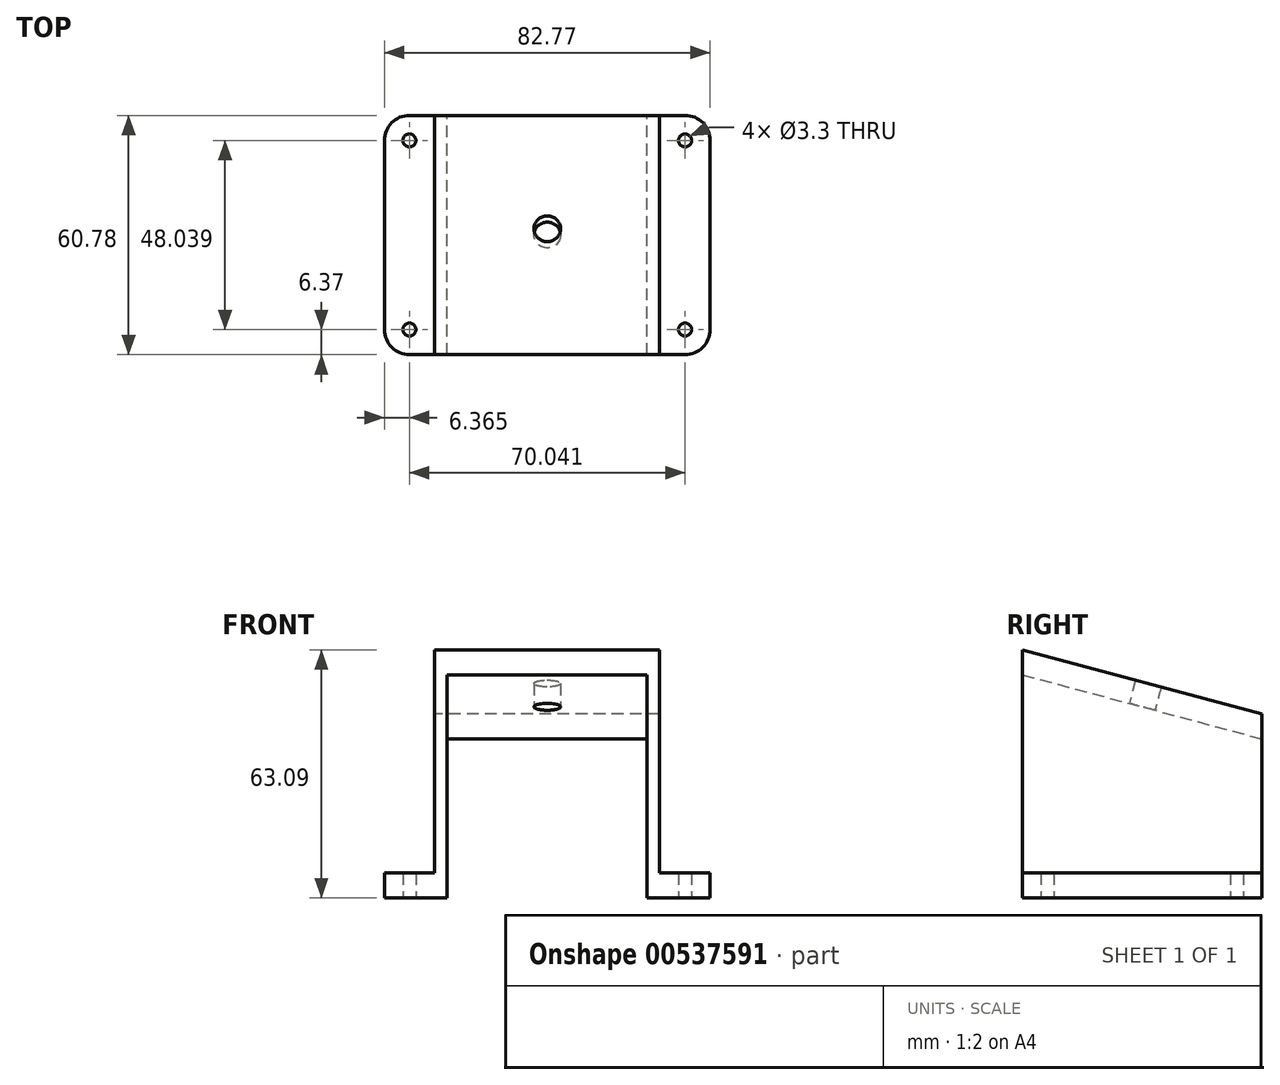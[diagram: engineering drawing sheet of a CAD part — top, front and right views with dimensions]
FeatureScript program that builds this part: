
annotation { "Feature Type Name" : "Feature", "Feature Type Description" : "" }
export const myFeature = defineFeature(function(context is Context, id is Id, definition is map)
    precondition{}
    {
        {
            var Q0;
            Q0=qCreatedBy(makeId("Top.planeOp"),FACE);
            var sketch = newSketch(context, id + "F0", { "sketchPlane" : qUnion([Q0])});
            skLineSegment(sketch, "E0", {"start": v(0, 0) * mm, "end": v(0, 30.39) * mm});
            skLineSegment(sketch, "E1", {"start": v(0, 30.39) * mm, "end": v(-6.45, 30.39) * mm});
            skArc(sketch, "E2", {"start": v(-6.45, 30.39) * mm, "mid": v(-10.95, 28.52) * mm, "end": v(-12.81, 24.02) * mm});
            skLineSegment(sketch, "E3", {"start": v(-12.81, 24.02) * mm, "end": v(-6.45, 24.02) * mm});
            skLineSegment(sketch, "E4", {"start": v(-6.45, 30.39) * mm, "end": v(-6.45, 24.02) * mm});
            skLineSegment(sketch, "E5", {"start": v(-12.81, 24.02) * mm, "end": v(-12.81, 0) * mm});
            skLineSegment(sketch, "E6.MirrorCS", {"start": v(-12.81, -24.02) * mm, "end": v(-12.81, 0) * mm});
            skArc(sketch, "E7.MirrorCS", {"start": v(-6.45, -30.39) * mm, "mid": v(-10.95, -28.52) * mm, "end": v(-12.81, -24.02) * mm});
            skLineSegment(sketch, "E8.MirrorCS", {"start": v(0, -30.39) * mm, "end": v(-6.45, -30.39) * mm});
            skLineSegment(sketch, "E9.MirrorCS", {"start": v(0, 0) * mm, "end": v(0, -30.39) * mm});
            skSolve(sketch);
        }
        {
            var Q0;
            Q0=makeQuery(id+"F0.imprint","IMPRINT",FACE,{"disambiguationData":[TD([[makeQuery(id+"F0.imprint","IMPRINT",EDGE,{"derivedFrom":sQuery(id+"F0.wireOp",EDGE,"E0")}),1.0]])]});
            var Q1;
            {var subQ0=sQuery(id+"F0.wireOp",EDGE,"E2");Q1=makeQuery(id+"F0.imprint","IMPRINT",FACE,{"disambiguationData":[TD([[makeQuery(id+"F0.imprint","IMPRINT",EDGE,{"derivedFrom":subQ0}),1.0]])]});}
            extrude(context, id + "F1", {"entities" : qUnion([Q0, Q1]), "depth" : 6.35 * mm, "offsetDistance" : 25.4 * mm});
        }
        {
            var Q0;
            Q0=qCreatedBy(makeId("Right.planeOp"),FACE);
            var sketch = newSketch(context, id + "F2", { "sketchPlane" : qUnion([Q0])});
            skLineSegment(sketch, "E10.0", {"start": v(-30.39, 6.35) * mm, "end": v(-30.39, 0) * mm});
            skLineSegment(sketch, "E11.0", {"start": v(30.39, 6.35) * mm, "end": v(30.39, 0) * mm});
            skLineSegment(sketch, "E12.bottom", {"start": v(-30.39, 6.35) * mm, "end": v(30.39, 6.35) * mm});
            skLineSegment(sketch, "E12.top", {"start": v(-30.39, 46.8) * mm, "end": v(30.39, 46.8) * mm});
            skLineSegment(sketch, "E12.left", {"start": v(-30.39, 6.35) * mm, "end": v(-30.39, 46.8) * mm});
            skLineSegment(sketch, "E12.right", {"start": v(30.39, 6.35) * mm, "end": v(30.39, 46.8) * mm});
            skLineSegment(sketch, "E13", {"start": v(-30.39, 46.8) * mm, "end": v(-30.39, 63.1) * mm});
            skLineSegment(sketch, "E14", {"start": v(-30.39, 63.1) * mm, "end": v(30.39, 46.8) * mm});
            skSolve(sketch);
        }
        {
            var Q0;
            Q0=makeQuery(id+"F2.imprint","IMPRINT",FACE,{"disambiguationData":[TD([[makeQuery(id+"F2.imprint","IMPRINT",EDGE,{"derivedFrom":sQuery(id+"F2.wireOp",EDGE,"E12.bottom")}),1.0]])]});
            var Q1;
            Q1=makeQuery(id+"F2.imprint","IMPRINT",FACE,{"disambiguationData":[TD([[makeQuery(id+"F2.imprint","IMPRINT",EDGE,{"derivedFrom":sQuery(id+"F2.wireOp",EDGE,"E12.top")}),1.0]])]});
            var Q2;
            Q2=makeQuery(id+"F1.opExtrude","SWEPT_FACE",FACE,{"disambiguationData":[OSD([sQuery(id+"F0.wireOp",EDGE,"E0"),sQuery(id+"F0.wireOp",EDGE,"E9.MirrorCS")])]});
            extrude(context, id + "F3", {"entities" : qUnion([Q0, Q1, Q2]), "operationType" : NewBodyOperationType.ADD, "depth" : 3.17 * mm, "offsetDistance" : 25.4 * mm});
        }
        {
            var Q0;
            Q0=makeQuery(id+"F3.boolean.opBoolean","MERGE",FACE,{"derivedFrom":[makeQuery(id+"F3.opExtrude","CAP_FACE",FACE,{"disambiguationData":[OSD([sQuery(id+"F0.wireOp",EDGE,"E0"),sQuery(id+"F0.wireOp",EDGE,"E9.MirrorCS")])],"isStart":false}),makeQuery(id+"F3.opExtrude","CAP_FACE",FACE,{"disambiguationData":[OSD([sQuery(id+"F2.wireOp",EDGE,"E12.bottom"),sQuery(id+"F2.wireOp",EDGE,"E12.left"),sQuery(id+"F2.wireOp",EDGE,"E12.right"),sQuery(id+"F2.wireOp",EDGE,"E13"),sQuery(id+"F2.wireOp",EDGE,"E14")])],"isStart":false})]});
            var sketch = newSketch(context, id + "F4", { "sketchPlane" : qUnion([Q0])});
            skLineSegment(sketch, "E15", {"start": v(-30.39, 56.74) * mm, "end": v(30.39, 40.46) * mm});
            skLineSegment(sketch, "E16.0", {"start": v(-30.39, 63.1) * mm, "end": v(-30.39, 0) * mm});
            skLineSegment(sketch, "E17.0", {"start": v(-30.39, 63.1) * mm, "end": v(30.39, 46.8) * mm});
            skLineSegment(sketch, "E18.0", {"start": v(30.39, 46.8) * mm, "end": v(30.39, 0) * mm});
            skSolve(sketch);
        }
        {
            var Q0;
            {var subQ0=sQuery(id+"F4.wireOp",EDGE,"E15");Q0=makeQuery(id+"F4.imprint","IMPRINT",FACE,{"disambiguationData":[TD([[makeQuery(id+"F4.imprint","IMPRINT",EDGE,{"derivedFrom":subQ0}),1.0]])]});}
            extrude(context, id + "F5", {"entities" : qUnion([Q0]), "operationType" : NewBodyOperationType.ADD, "depth" : 25.4 * mm, "offsetDistance" : 25.4 * mm});
        }
        {
            var Q0;
            Q0=makeQuery(id+"F1.opExtrude","SWEPT_BODY",BODY,{"disambiguationData":[OSD([sQuery(id+"F0.wireOp",EDGE,"E0"),sQuery(id+"F0.wireOp",EDGE,"E1"),sQuery(id+"F0.wireOp",EDGE,"E2"),sQuery(id+"F0.wireOp",EDGE,"E5"),sQuery(id+"F0.wireOp",EDGE,"E6.MirrorCS"),sQuery(id+"F0.wireOp",EDGE,"E7.MirrorCS"),sQuery(id+"F0.wireOp",EDGE,"E8.MirrorCS"),sQuery(id+"F0.wireOp",EDGE,"E9.MirrorCS"),sQuery(id+"F0.wireOp",EDGE,"Jg3dPquB-hT7Z-jwV8-vggr-lBs4hWKGQJc3"),sQuery(id+"F0.wireOp",EDGE,"43ba567d-2faf-43e1-93f8-a82567d2d6100.MirrorC")])]});
            var Q1;
            Q1=makeQuery(id+"F5.opExtrude","CAP_FACE",FACE,{"disambiguationData":[OSD([sQuery(id+"F4.wireOp",EDGE,"E15"),sQuery(id+"F4.wireOp",EDGE,"E16.0"),sQuery(id+"F4.wireOp",EDGE,"E17.0"),sQuery(id+"F4.wireOp",EDGE,"E18.0")])],"isStart":false});
            mirror(context, id + "F6", {"operationType" : NewBodyOperationType.ADD, "entities" : qUnion([Q0]), "mirrorPlane" : qUnion([Q1])});
        }
        {
            var Q0;
            {var subQ0=makeQuery(id+"F5.opExtrude","SWEPT_FACE",FACE,{"disambiguationData":[OSD([sQuery(id+"F4.wireOp",EDGE,"E15")])]});Q0=makeQuery(id+"F6.boolean.opBoolean","MERGE",FACE,{"derivedFrom":[subQ0,makeQuery(id+"F6.opPattern","COPY",FACE,{"derivedFrom":subQ0,"instanceName":"1"})]});}
            var sketch = newSketch(context, id + "F7", { "sketchPlane" : qUnion([Q0])});
            skLineSegment(sketch, "E19", {"start": v(3.18, 12.58) * mm, "end": v(53.98, 12.58) * mm});
            skPoint(sketch, "E20", {"position": v(28.58, 12.58) * mm});
            skSolve(sketch);
        }
        {
            var Q0;
            Q0=sQuery(id+"F7.wireOp",VERTEX,"E20");
            var Q1;
            Q1=makeQuery(id+"F1.opExtrude","SWEPT_BODY",BODY,{"disambiguationData":[OSD([sQuery(id+"F0.wireOp",EDGE,"E0"),sQuery(id+"F0.wireOp",EDGE,"E1"),sQuery(id+"F0.wireOp",EDGE,"E2"),sQuery(id+"F0.wireOp",EDGE,"E5"),sQuery(id+"F0.wireOp",EDGE,"E6.MirrorCS"),sQuery(id+"F0.wireOp",EDGE,"E7.MirrorCS"),sQuery(id+"F0.wireOp",EDGE,"E8.MirrorCS"),sQuery(id+"F0.wireOp",EDGE,"E9.MirrorCS"),sQuery(id+"F0.wireOp",EDGE,"Jg3dPquB-hT7Z-jwV8-vggr-lBs4hWKGQJc3"),sQuery(id+"F0.wireOp",EDGE,"43ba567d-2faf-43e1-93f8-a82567d2d6100.MirrorC")])]});
            hole(context, id + "F8", {"style" : HoleStyle.SIMPLE, "endStyle" : HoleEndStyle.THROUGH, "standardTappedOrClearance" : lookupTablePath({ "standard" : "ANSI", "fit" : "Normal (ASME)", "size" : "1/4", "type" : "Clearance" }), "standardBlindInLast" : lookupTablePath({ "fit" : "Free", "standard" : "ANSI", "size" : "1/4", "type" : "Clearance" }), "holeDiameter" : 6.76 * mm, "tappedDepth" : 7.85 * mm, "tapClearance" : 6, "locations" : qUnion([Q0]), "scope" : qUnion([Q1])});
        }
        {
            var Q0;
            Q0=qCreatedBy(makeId("Top.planeOp"),FACE);
            var sketch = newSketch(context, id + "F9", { "sketchPlane" : qUnion([Q0])});
            skArc(sketch, "E21.0", {"start": v(-6.45, -30.39) * mm, "mid": v(-10.95, -28.52) * mm, "end": v(-12.81, -24.02) * mm});
            skArc(sketch, "E22.0", {"start": v(-6.45, 30.39) * mm, "mid": v(-10.95, 28.52) * mm, "end": v(-12.81, 24.02) * mm});
            skArc(sketch, "E23.0", {"start": v(63.6, 30.39) * mm, "mid": v(68.1, 28.52) * mm, "end": v(69.96, 24.02) * mm});
            skArc(sketch, "E24.0", {"start": v(63.6, -30.39) * mm, "mid": v(68.1, -28.52) * mm, "end": v(69.96, -24.02) * mm});
            skSolve(sketch);
        }
        {
            var Q0;
            Q0=sQuery(id+"F9.wireOp",VERTEX,"E21.0.center");
            var Q1;
            Q1=sQuery(id+"F9.wireOp",VERTEX,"E22.0.center");
            var Q2;
            Q2=sQuery(id+"F9.wireOp",VERTEX,"E23.0.center");
            var Q3;
            Q3=sQuery(id+"F9.wireOp",VERTEX,"E24.0.center");
            var Q4;
            Q4=makeQuery(id+"F1.opExtrude","SWEPT_BODY",BODY,{"disambiguationData":[OSD([sQuery(id+"F0.wireOp",EDGE,"E0"),sQuery(id+"F0.wireOp",EDGE,"E1"),sQuery(id+"F0.wireOp",EDGE,"E2"),sQuery(id+"F0.wireOp",EDGE,"E5"),sQuery(id+"F0.wireOp",EDGE,"E6.MirrorCS"),sQuery(id+"F0.wireOp",EDGE,"E7.MirrorCS"),sQuery(id+"F0.wireOp",EDGE,"E8.MirrorCS"),sQuery(id+"F0.wireOp",EDGE,"E9.MirrorCS")])]});
            hole(context, id + "F10", {"style" : HoleStyle.SIMPLE, "endStyle" : HoleEndStyle.THROUGH, "oppositeDirection" : true, "standardTappedOrClearance" : lookupTablePath({ "standard" : "ISO", "fit" : "Normal", "size" : "M3", "type" : "Clearance" }), "standardBlindInLast" : lookupTablePath({ "fit" : "Standard", "standard" : "ISO", "size" : "M3", "type" : "Clearance" }), "holeDiameter" : 3.3 * mm, "tappedDepth" : 7.85 * mm, "tapClearance" : 6, "locations" : qUnion([Q0, Q1, Q2, Q3]), "scope" : qUnion([Q4])});
        }
    });
